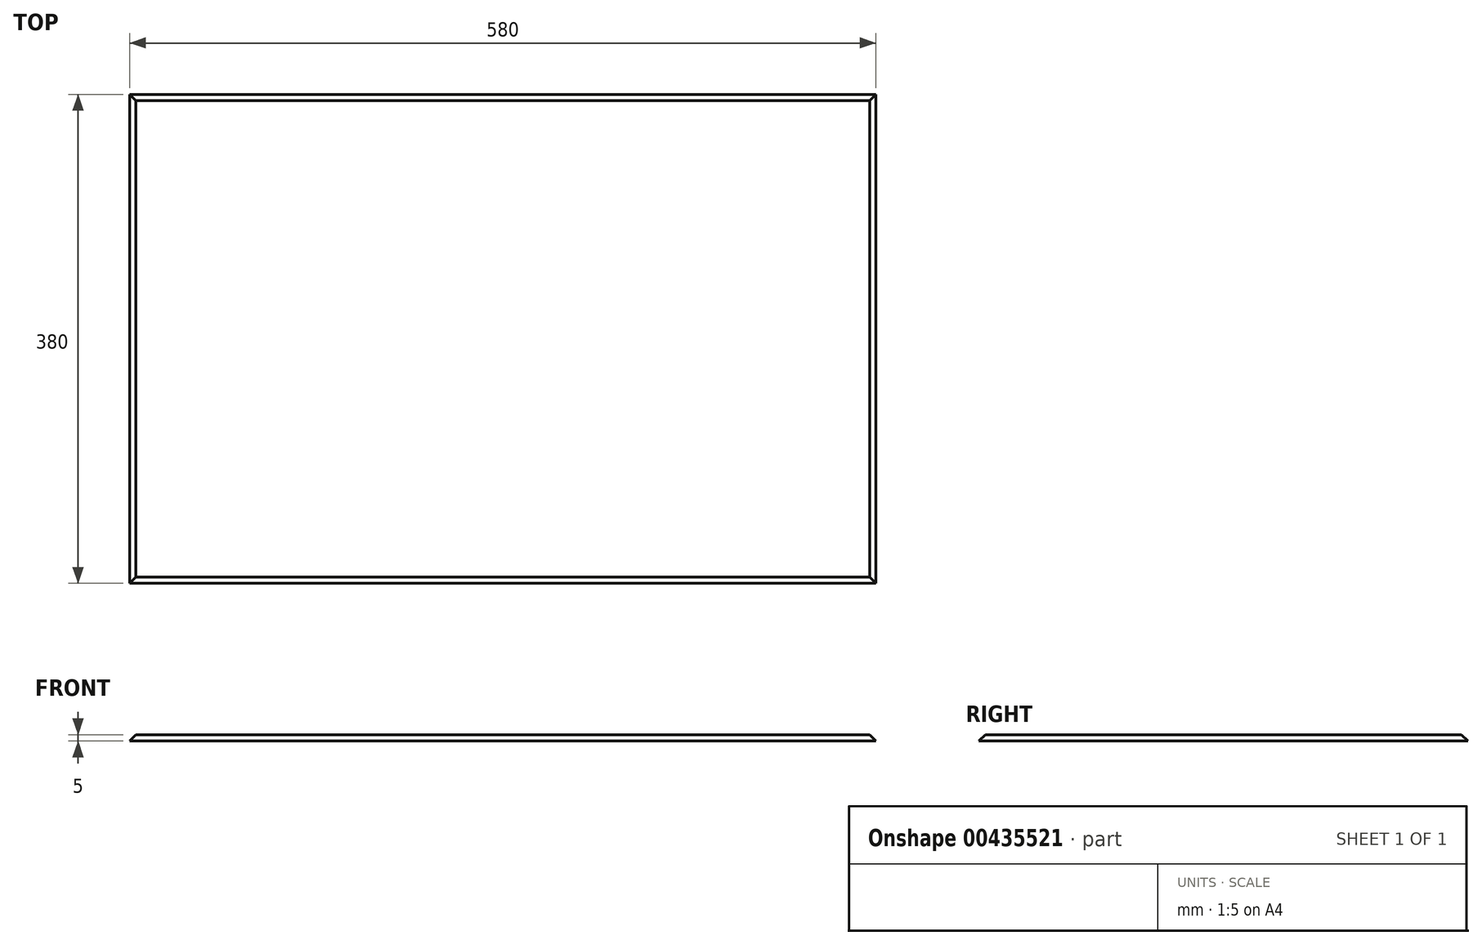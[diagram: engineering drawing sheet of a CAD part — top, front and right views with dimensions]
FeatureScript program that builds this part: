
annotation { "Feature Type Name" : "Feature", "Feature Type Description" : "" }
export const myFeature = defineFeature(function(context is Context, id is Id, definition is map)
    precondition{}
    {
        {
            var Q0;
            Q0=qCreatedBy(makeId("Top.planeOp"),FACE);
            var sketch = newSketch(context, id + "F0", { "sketchPlane" : qUnion([Q0])});
            skLineSegment(sketch, "E0.bottom", {"start": v(-290, 190) * mm, "end": v(290, 190) * mm});
            skLineSegment(sketch, "E0.top", {"start": v(-290, -190) * mm, "end": v(290, -190) * mm});
            skLineSegment(sketch, "E0.left", {"start": v(-290, 190) * mm, "end": v(-290, -190) * mm});
            skLineSegment(sketch, "E0.right", {"start": v(290, 190) * mm, "end": v(290, -190) * mm});
            skPoint(sketch, "E0.middle", {"position": v(0, 0) * mm});
            skSolve(sketch);
        }
        {
            var Q0;
            Q0=makeQuery(id+"F0.imprint","IMPRINT",FACE,{"disambiguationData":[TD([[makeQuery(id+"F0.imprint","IMPRINT",EDGE,{"derivedFrom":sQuery(id+"F0.wireOp",EDGE,"E0.bottom")}),-1.0]])]});
            extrude(context, id + "F1", {"entities" : qUnion([Q0]), "depth" : 5 * mm});
        }
        {
            var Q0;
            Q0=makeQuery(id+"F1.opExtrude","CAP_FACE",FACE,{"disambiguationData":[OSD([sQuery(id+"F0.wireOp",EDGE,"E0.bottom"),sQuery(id+"F0.wireOp",EDGE,"E0.top"),sQuery(id+"F0.wireOp",EDGE,"E0.left"),sQuery(id+"F0.wireOp",EDGE,"E0.right")])],"isStart":false});
            chamfer(context, id + "F2", {"entities" : qUnion([Q0]), "width" : 5 * mm, "tangentPropagation" : true});
        }
    });
